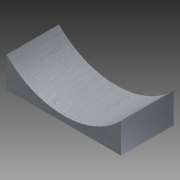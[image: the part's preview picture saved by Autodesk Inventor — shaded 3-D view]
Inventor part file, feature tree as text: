
AUTODESK INVENTOR PART (.ipt)
format: ipt  version: 2011 SP1 (Build 150282100, 282)  size: 86,528 bytes
history: native  units: in
note: dims shown in document units (in); Inventor stores cm internally (conversion verified against a paired STEP export)
features: extrude x1, sketch x1
ambient origin geometry x8: Origin, YZ Plane, XZ Plane, XY Plane, X Axis, Y Axis, Z Axis, Center Point
bodies: Solid1 (feature_tree)
feature tree (2):
  extrude  "Extrusion1"  Depth=6.0in
  sketch  "Sketch1"  dims[d0=4.1875in d1=6.0in d2=0.3125in d3=2.75in d4=0.0in]
